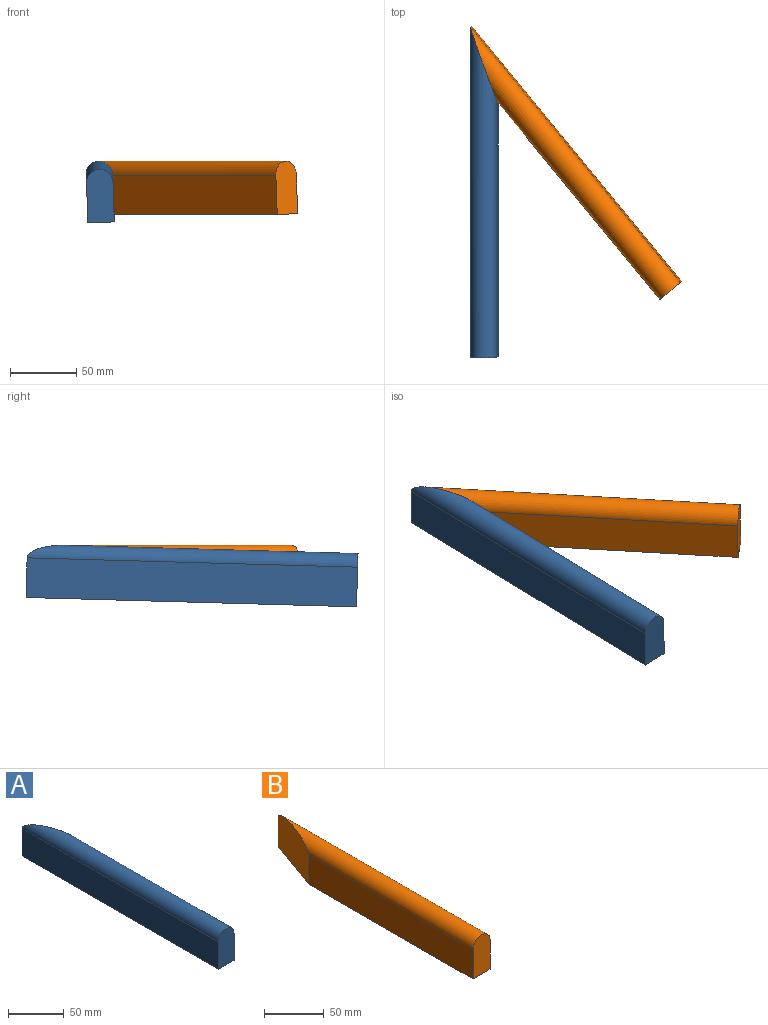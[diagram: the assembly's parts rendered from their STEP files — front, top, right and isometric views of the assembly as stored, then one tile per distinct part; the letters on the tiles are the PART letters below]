
ASSEMBLY  parts=2 mates=1
PART A: 6 faces, bbox 20x250x40 mm
  f0: plane 194.16x30mm, normal (1,0,0), area 5824.7mm2, adj f1,f3,f4,f5
  f1: cylinder r=10mm len=250mm, axis (0,1,0), area 6976.8mm2, adj f0,f2,f4,f5
  f2: plane 250x30mm, normal (-1,0,0), area 7500mm2, adj f1,f3,f4,f5
  f3: plane 250x20mm, normal (0,0,-1), area 4441.6mm2, adj f0,f2,f4,f5
  f4: plane 40x20mm, normal (0,-1,0), area 757.1mm2, adj f0,f1,f2,f3
  f5: plane 55.84x40mm, normal (0.94,0.34,0), area 2245.4mm2, adj f0,f1,f2,f3
PART B: 6 faces, bbox 20x250x40 mm
  f0: plane 194.16x30mm, normal (-1,0,0), area 5824.7mm2, adj f1,f3,f4,f5
  f1: plane 250x20mm, normal (0,0,-1), area 4441.6mm2, adj f0,f2,f4,f5
  f2: plane 250x30mm, normal (1,0,0), area 7500mm2, adj f1,f3,f4,f5
  f3: cylinder r=10mm len=250mm, axis (0,1,0), area 6976.8mm2, adj f0,f2,f4,f5
  f4: plane 40x20mm, normal (0,-1,0), area 757.1mm2, adj f0,f1,f2,f3
  f5: plane 55.84x40mm, normal (-0.94,0.34,0), area 2245.4mm2, adj f0,f1,f2,f3
PLACE A rot(axis=(0.63,-0.77,0),2.5deg) t=(42.86,22.48,-65.16)mm
PLACE B rot(axis=(0.02,-0.06,1),39.5deg) t=(27.42,9.79,-66.05)mm
MATE fastened B.f5 <-> A.f5  axis (-0.94,-0.34,-0.04) through (52.22,-5.97,-46.63)mm
